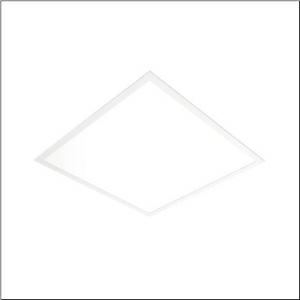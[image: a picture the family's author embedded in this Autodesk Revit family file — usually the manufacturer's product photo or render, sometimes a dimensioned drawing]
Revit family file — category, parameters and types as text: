
# Revit family: apollon_r__41_51mh12wm2443_7fd9
name_source: partatom
category: Lighting Fixtures
units: mm (PartAtom-declared; Revit-internal decimal feet)

## family parameters
Cut with Voids When Loaded = No
Host = Face
Light Source = No
Part Type = Normal
Room Calculation Point = No
Round Connector Dimension = Use Diameter
Shared = No

## types (1)
- --- (1 x LED, 4380 lm, 35 W, 4000K)
    Apparent Load = 35 VA
    CIE Flux Codes = 61 87 97 100 100
    Color Rendering = 80
    Color Temperature = 4000K
    Default Elevation = 1800 mm
    Description = Apollon® 41, office luminaire, primary optical cover: prismatic diffuser, of PS, light emission: direct distribution, primary light characteristic: symmetric, installation type: lay-in mounting, LED, rated luminous flux: 4.375lm, luminous efficacy: 125lm/W, light colour: 840, colour temperature: 4000K, control gear: ON/OFF Multilumen, with terminal, 3-pole, mains connection: 220..240V, AC, 50/60Hz, rated input power: 35W, housing, of aluminium section, traffic white (RAL 9016), module: M600, length: 595mm, width: 595mm, height: 60mm, recess depth: 180mm, housing upper side, of sheet steel, protection rating (complete): IP20, protection rating (lamp compartment, on room side): IP40, insulation class (complete): insulation class II (safety insulation), certification: CE, ENEC, impact resistance: IK03, permissible operating ambient temperature: -25..+40°C, packaging unit: 1 piece
    Height = 0 mm  [stored 0 ft]
    Lamp = 1 x LED
    Lamp Light Flux = 4380 lm
    Lamp Power = 35 W
    Lamp count = 1
    Length = 600 mm
    Luminous efficacy = 125 lm/W
    Manufacturer = Siteco
    ModVariant = No
    Model = 51MH12WM2443
    Mounting Place = Ceiling
    Mounting Type = Recessed
    Number of Poles = 1
    OnlyDefault = Yes
    Power Factor = 1
    Product Name = Apollon® 41
    Product group = office luminaire | ceiling recessed
    ProductGroupID = 401
    Protection Class = Protection class II
    Protection Degree = IP 20
    RLX_Detail_Level = 1
    RLX_Emergency_Light_Flux = 0 lm
    RLX_Emergency_Type = 0
    RLX_Emergency_Type_DB = No
    RlxData = <blob elided: 12989 chars, md5=0ef9b356>
    Socket = socket
    Standby Power = 0 W
    System Light Flux = 4380 lm
    System Power = 35 W
    Type Comments = factory setting: luminous flux: 100 % | (ON | ON) | 900 mA
    Type Image = l_1291024.jpg
    URL = http://relux.com
    VarID = @adj_013655
    Voltage = 0 V
    Weight = 0.00 kg
    Width = 600 mm

note: [stored X ft] marks values corroborated as IEEE doubles in the binary element streams (Revit-internal decimal feet)

## geometry (parser evidence)
native form markers: Sweep x11
no freeform markers — native parametric forms only
